# Revit family: Hager-Univers-IP44-D205-H1250-Cl.I-Encl-NoHosted-CH-it
name_source: partatom
category: Electrical Equipment
units: mm (PartAtom-declared; Revit-internal decimal feet)

## family parameters
Always vertical = Yes
Cut with Voids When Loaded = No
Panel Configuration = Two Columns, Circuits Across
Part Type = Panelboard
Room Calculation Point = No
Round Connector Dimension = Use Diameter
Shared = No
Work Plane-Based = Yes

## types (10) — shared parameters
Default Elevation = 1219 mm  [stored 3.99934 ft]
EF000003 - Tipo di montaggio = EV000384 - A parete
EF000007 - colore = EV000202 - bianco
EF000040 - Altezza = 1250 mm  [stored 4.10105 ft]
EF000049 - profondità = 205 mm  [stored 0.672572 ft]
EF000116 - numero RAL = 9010
EF000118 - con piastra di montaggio = No
EF000266 - numero di file = 8
EF000339 - tipo di copertura = EV001012 - coperchio
EF001088 - possibilità di applicazione = Yes
EF001131 - profondità interna = 130 mm  [stored 0.426509 ft]
EF001596 - Attacco Lampada = EV000179 - acciaio
EF001613 - Integrità del circuito = EV000494 - senza
EF003532 - adatto per uso esterno = No
EF004293 - resistenza agli urti = EV006815 - IK09
EF005474 - grado di protezione (IP) = EV006418 - IP44
EF006244 - coperchio/porta trasparente = No
EF006306 - con serratura = No
EF007800 - adatto per parafulmine = No
EF008873 - corrente nominale (In) = 250 A
EF009170 - spessore materiale scatola = 1 mm  [stored 0.00328084 ft]
EF009171 - spessore materiale porta/coperchio = 1 mm  [stored 0.00328084 ft]
EF009212 - esecuzione coperchio = EV000116 - chiuso
EF015940 - Coprire con rilascio di sovrapressione = No
HG000002 - Con porta = Yes
HG000003 - Gamma = Univers
HG000006 - Ad incasso = No
HG000023 - Custodia a doppia sezione = No
HG000024 - Altezza della sezione inferiore = 600 mm
HG000026 - A pavimento = No
Manufacturer = Hager
Type Comments = Univers
zero-valued in all types: HG000027 - Altezza dello zoccolo

## per-type parameters (varying)
| type | EF000008 - Larghezza | EF000218 - profondità di incasso | EF000437 - numero di ingressi per conduttori | EF002950 - Numero moduli DIN | EF004427 - numero di moduli | EF004464 - tipo di porta | EF009554 - numero delle aperture per la piastra della flangia | HG000004 - Codice produttore | HG000009 - Porta doppia a battente | HG000010 - Porte asimmetriche |
| A parete IP44 L1050 A1250 P205  - FP84QT | 1050 mm | 0 mm  [stored 0 ft] | 8 | 48 | 384 | EV003602 - doppio | 8 | FP84QT | No | No |
| A parete IP44 L1050 A1250 P205  - FP84TN2 | 1050 mm | 205 mm  [stored 0.672572 ft] | 8 | 48 | 384 | EV003602 - doppio | 8 | FP84TN2 | Yes | No |
| A parete IP44 L1300 A1250 P205  - FP85QT | 1300 mm  [stored 4.26509 ft] | 0 mm  [stored 0 ft] | 10 | 60 | 480 | EV003602 - doppio | 10 | FP85QT | No | No |
| A parete IP44 L1300 A1250 P205  - FP85TN2 | 1300 mm  [stored 4.26509 ft] | 205 mm  [stored 0.672572 ft] | 10 | 60 | 480 | EV003602 - doppio | 10 | FP85TN2 | Yes | Yes |
| A parete IP44 L300 A1250 P205  - FP81QT | 300 mm | 0 mm  [stored 0 ft] | 2 | 12 | 96 | EV002646 - singolo | 2 | FP81QT | No | No |
| A parete IP44 L300 A1250 P205  - FP81TN2 | 300 mm | 205 mm  [stored 0.672572 ft] | 2 | 12 | 96 | EV002646 - singolo | 2 | FP81TN2 | No | No |
| A parete IP44 L550 A1250 P205  - FP82QT | 550 mm | 0 mm  [stored 0 ft] | 4 | 24 | 192 | EV002646 - singolo | 4 | FP82QT | No | No |
| A parete IP44 L550 A1250 P205  - FP82TN2 | 550 mm | 205 mm  [stored 0.672572 ft] | 4 | 24 | 192 | EV002646 - singolo | 4 | FP82TN2 | No | No |
| A parete IP44 L800 A1250 P205  - FP83QT | 800 mm  [stored 2.62467 ft] | 0 mm  [stored 0 ft] | 6 | 36 | 288 | EV002646 - singolo | 6 | FP83QT | No | No |
| A parete IP44 L800 A1250 P205  - FP83TN2 | 800 mm  [stored 2.62467 ft] | 205 mm  [stored 0.672572 ft] | 6 | 36 | 288 | EV002646 - singolo | 6 | FP83TN2 | No | No |

note: [stored X ft] marks values corroborated as IEEE doubles in the binary element streams (Revit-internal decimal feet)

## geometry (parser evidence)
native form markers: Blend x4, Sweep x11
no freeform markers — native parametric forms only
